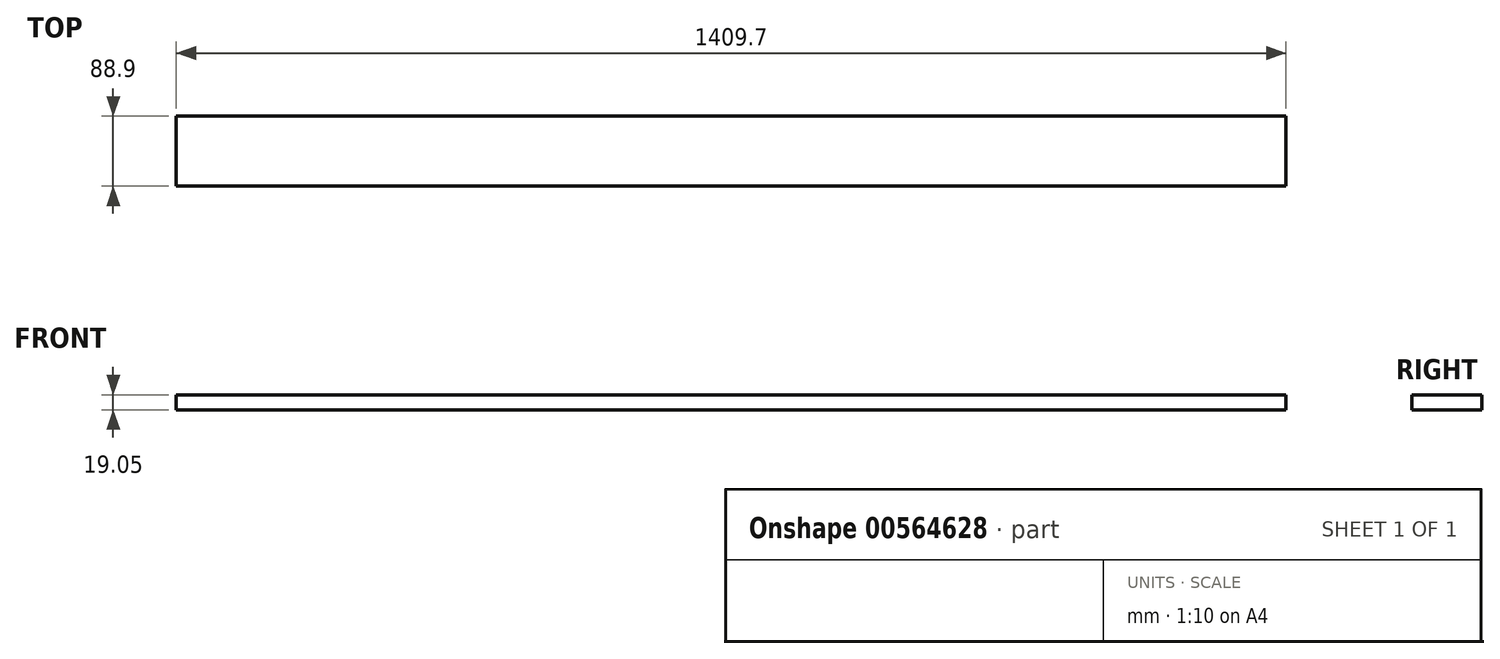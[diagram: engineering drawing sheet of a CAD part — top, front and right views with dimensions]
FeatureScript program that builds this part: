
annotation { "Feature Type Name" : "Feature", "Feature Type Description" : "" }
export const myFeature = defineFeature(function(context is Context, id is Id, definition is map)
    precondition{}
    {
        {
            var Q0;
            Q0=qCreatedBy(makeId("Top.planeOp"),FACE);
            var sketch = newSketch(context, id + "F0", { "sketchPlane" : qUnion([Q0])});
            skLineSegment(sketch, "E0.bottom", {"start": v(-704.85, 44.45) * mm, "end": v(704.85, 44.45) * mm});
            skLineSegment(sketch, "E0.top", {"start": v(-704.85, -44.45) * mm, "end": v(704.85, -44.45) * mm});
            skLineSegment(sketch, "E0.left", {"start": v(-704.85, 44.45) * mm, "end": v(-704.85, -44.45) * mm});
            skLineSegment(sketch, "E0.right", {"start": v(704.85, 44.45) * mm, "end": v(704.85, -44.45) * mm});
            skPoint(sketch, "E0.middle", {"position": v(0, 0) * mm});
            skSolve(sketch);
        }
        {
            var Q0;
            Q0=makeQuery(id+"F0.imprint","IMPRINT",FACE,{"disambiguationData":[TD([[makeQuery(id+"F0.imprint","IMPRINT",EDGE,{"derivedFrom":sQuery(id+"F0.wireOp",EDGE,"E0.bottom")}),-1.0]])]});
            extrude(context, id + "F1", {"entities" : qUnion([Q0]), "depth" : 19.05 * mm, "offsetDistance" : 25.4 * mm});
        }
    });
